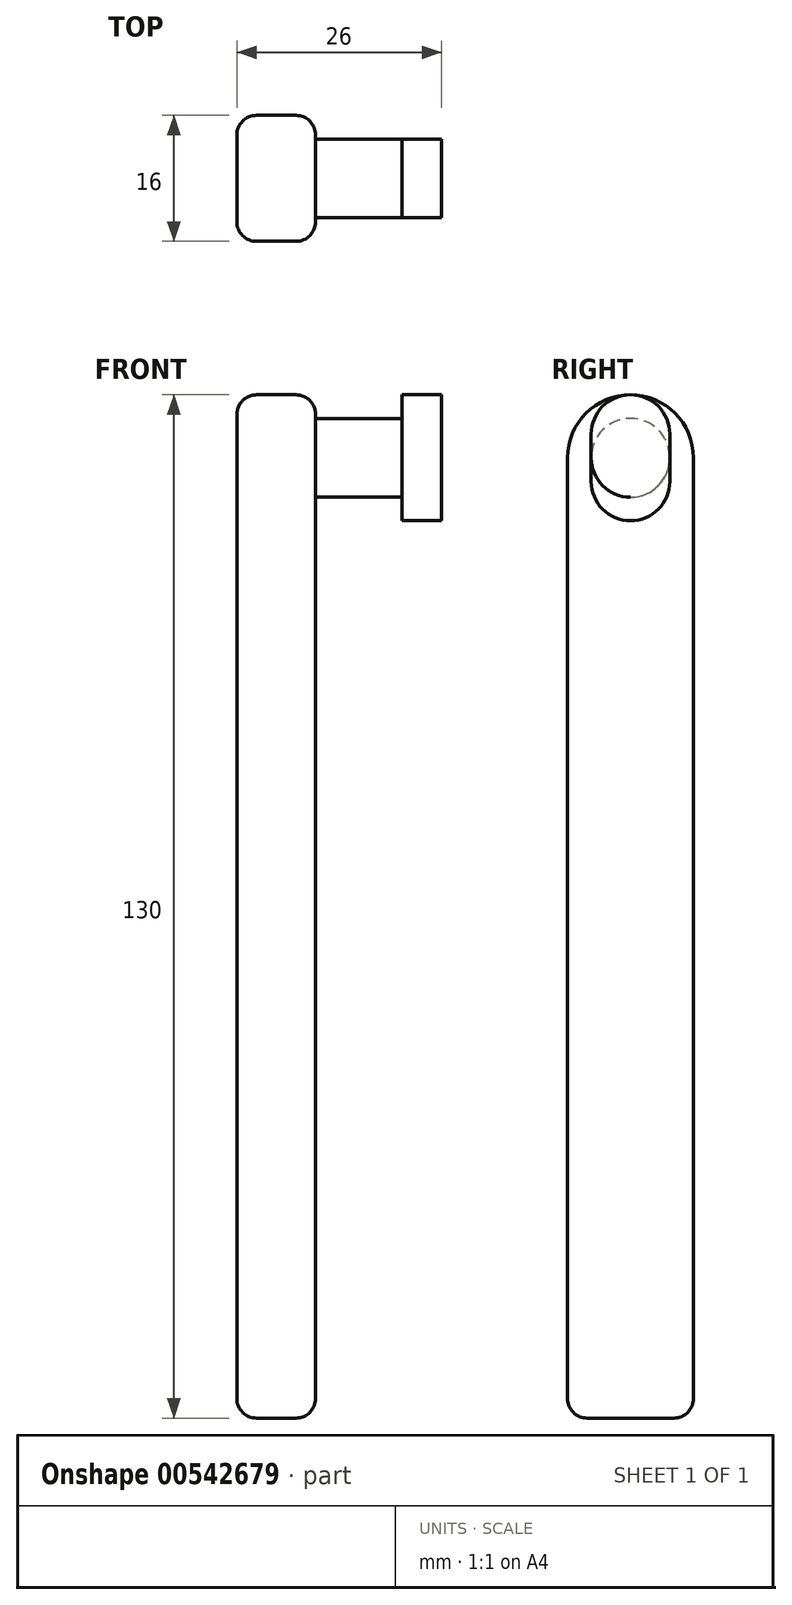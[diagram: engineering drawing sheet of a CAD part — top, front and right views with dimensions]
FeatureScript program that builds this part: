
annotation { "Feature Type Name" : "Feature", "Feature Type Description" : "" }
export const myFeature = defineFeature(function(context is Context, id is Id, definition is map)
    precondition{}
    {
        {
            var Q0;
            Q0=qCreatedBy(makeId("Right.planeOp"),FACE);
            var sketch = newSketch(context, id + "F0", { "sketchPlane" : qUnion([Q0])});
            skLineSegment(sketch, "E0.bottom", {"start": v(-8, 8) * mm, "end": v(8, 8) * mm});
            skLineSegment(sketch, "E0.top", {"start": v(-8, -122) * mm, "end": v(8, -122) * mm});
            skLineSegment(sketch, "E0.left", {"start": v(-8, 8) * mm, "end": v(-8, -122) * mm});
            skLineSegment(sketch, "E0.right", {"start": v(8, 8) * mm, "end": v(8, -122) * mm});
            skPoint(sketch, "E1", {"position": v(0, 8) * mm});
            skSolve(sketch);
        }
        {
            var Q0;
            Q0 = qSketchRegion(id + "F0", true);
            extrude(context, id + "F1", {"entities" : qUnion([Q0]), "depth" : 10 * mm, "offsetDistance" : 25 * mm});
        }
        {
            var Q0;
            Q0=makeQuery(id+"F1.opExtrude","CAP_FACE",FACE,{"disambiguationData":[OSD([sQuery(id+"F0.wireOp",EDGE,"E0.bottom"),sQuery(id+"F0.wireOp",EDGE,"E0.top"),sQuery(id+"F0.wireOp",EDGE,"E0.left"),sQuery(id+"F0.wireOp",EDGE,"E0.right")])],"isStart":false});
            var sketch = newSketch(context, id + "F2", { "sketchPlane" : qUnion([Q0])});
            skCircle(sketch, "E2", {"center": v(0, 0) * mm, "radius": 5 * mm});
            skSolve(sketch);
        }
        {
            var Q0;
            Q0 = qSketchRegion(id + "F2", true);
            extrude(context, id + "F3", {"entities" : qUnion([Q0]), "operationType" : NewBodyOperationType.ADD, "depth" : 11 * mm, "offsetDistance" : 25 * mm});
        }
        {
            var Q0;
            Q0=makeQuery(id+"F3.opExtrude","CAP_FACE",FACE,{"disambiguationData":[OSD([sQuery(id+"F2.wireOp",EDGE,"E2")])],"isStart":false});
            var sketch = newSketch(context, id + "F4", { "sketchPlane" : qUnion([Q0])});
            skLineSegment(sketch, "E3.bottom", {"start": v(-5, -8) * mm, "end": v(5, -8) * mm});
            skLineSegment(sketch, "E3.top", {"start": v(-5, 8) * mm, "end": v(5, 8) * mm});
            skLineSegment(sketch, "E3.left", {"start": v(-5, -8) * mm, "end": v(-5, 8) * mm});
            skLineSegment(sketch, "E3.right", {"start": v(5, -8) * mm, "end": v(5, 8) * mm});
            skPoint(sketch, "E3.middle", {"position": v(0, 0) * mm});
            skSolve(sketch);
        }
        {
            var Q0;
            Q0 = qSketchRegion(id + "F4", true);
            extrude(context, id + "F5", {"entities" : qUnion([Q0]), "operationType" : NewBodyOperationType.ADD, "depth" : 5 * mm, "offsetDistance" : 25 * mm});
        }
        {
            var Q0;
            Q0=makeQuery(id+"F1.opExtrude","SWEPT_EDGE",EDGE,{"disambiguationData":[OSD([sQuery(id+"F0.wireOp",EDGE,"E0.bottom"),sQuery(id+"F0.wireOp",EDGE,"E0.left")])]});
            var Q1;
            Q1=makeQuery(id+"F1.opExtrude","SWEPT_EDGE",EDGE,{"disambiguationData":[OSD([sQuery(id+"F0.wireOp",EDGE,"E0.bottom"),sQuery(id+"F0.wireOp",EDGE,"E0.right")])]});
            fillet(context, id + "F6", {"entities" : qUnion([Q0, Q1]), "radius" : 8 * mm, "tangentPropagation" : true, "allowEdgeOverflow" : false});
        }
        {
            var Q0;
            Q0=makeQuery(id+"F5.opExtrude","SWEPT_EDGE",EDGE,{"disambiguationData":[OSD([sQuery(id+"F4.wireOp",EDGE,"E3.top"),sQuery(id+"F4.wireOp",EDGE,"E3.left")])]});
            var Q1;
            Q1=makeQuery(id+"F5.opExtrude","SWEPT_EDGE",EDGE,{"disambiguationData":[OSD([sQuery(id+"F4.wireOp",EDGE,"E3.top"),sQuery(id+"F4.wireOp",EDGE,"E3.right")])]});
            var Q2;
            Q2=makeQuery(id+"F5.opExtrude","SWEPT_EDGE",EDGE,{"disambiguationData":[OSD([sQuery(id+"F4.wireOp",EDGE,"E3.bottom"),sQuery(id+"F4.wireOp",EDGE,"E3.left")])]});
            var Q3;
            Q3=makeQuery(id+"F5.opExtrude","SWEPT_EDGE",EDGE,{"disambiguationData":[OSD([sQuery(id+"F4.wireOp",EDGE,"E3.bottom"),sQuery(id+"F4.wireOp",EDGE,"E3.right")])]});
            fillet(context, id + "F7", {"entities" : qUnion([Q0, Q1, Q2, Q3]), "radius" : 5 * mm, "tangentPropagation" : true, "allowEdgeOverflow" : false});
        }
        {
            var Q0;
            {var subQ0=sQuery(id+"F4.wireOp",EDGE,"E3.right");var subQ1=sQuery(id+"F4.wireOp",EDGE,"E3.top");Q0=makeQuery(id+"F7.opFillet","BLEND_EDGE",EDGE,{"blendedFrom":[makeQuery(id+"F5.opExtrude","SWEPT_EDGE",EDGE,{"disambiguationData":[OSD([subQ1,subQ0])]}),makeQuery(id+"F5.opExtrude","CAP_FACE",FACE,{"disambiguationData":[OSD([sQuery(id+"F4.wireOp",EDGE,"E3.bottom"),subQ1,sQuery(id+"F4.wireOp",EDGE,"E3.left"),subQ0])],"isStart":false})],"blendedInto":[makeQuery(id+"F5.opExtrude","CAP_FACE",FACE,{"disambiguationData":[OSD([sQuery(id+"F4.wireOp",EDGE,"E3.bottom"),subQ1,sQuery(id+"F4.wireOp",EDGE,"E3.left"),subQ0])],"isStart":false})]});}
            var Q1;
            {var subQ0=sQuery(id+"F0.wireOp",EDGE,"E0.left");var subQ1=sQuery(id+"F0.wireOp",EDGE,"E0.bottom");Q1=makeQuery(id+"F6.opFillet","BLEND_EDGE",EDGE,{"blendedFrom":[makeQuery(id+"F1.opExtrude","SWEPT_EDGE",EDGE,{"disambiguationData":[OSD([subQ1,subQ0])]}),makeQuery(id+"F1.opExtrude","CAP_FACE",FACE,{"disambiguationData":[OSD([subQ1,sQuery(id+"F0.wireOp",EDGE,"E0.top"),subQ0,sQuery(id+"F0.wireOp",EDGE,"E0.right")])],"isStart":false})],"blendedInto":[makeQuery(id+"F1.opExtrude","CAP_FACE",FACE,{"disambiguationData":[OSD([subQ1,sQuery(id+"F0.wireOp",EDGE,"E0.top"),subQ0,sQuery(id+"F0.wireOp",EDGE,"E0.right")])],"isStart":false})]});}
            var Q2;
            {var subQ0=sQuery(id+"F0.wireOp",EDGE,"E0.left");var subQ1=sQuery(id+"F0.wireOp",EDGE,"E0.bottom");Q2=makeQuery(id+"F6.opFillet","BLEND_EDGE",EDGE,{"blendedFrom":[makeQuery(id+"F1.opExtrude","SWEPT_EDGE",EDGE,{"disambiguationData":[OSD([subQ1,subQ0])]}),makeQuery(id+"F1.opExtrude","CAP_FACE",FACE,{"disambiguationData":[OSD([subQ1,sQuery(id+"F0.wireOp",EDGE,"E0.top"),subQ0,sQuery(id+"F0.wireOp",EDGE,"E0.right")])],"isStart":true})],"blendedInto":[makeQuery(id+"F1.opExtrude","CAP_FACE",FACE,{"disambiguationData":[OSD([subQ1,sQuery(id+"F0.wireOp",EDGE,"E0.top"),subQ0,sQuery(id+"F0.wireOp",EDGE,"E0.right")])],"isStart":true})]});}
            var Q3;
            Q3=makeQuery(id+"F1.opExtrude","CAP_EDGE",EDGE,{"disambiguationData":[OSD([sQuery(id+"F0.wireOp",EDGE,"E0.top")])],"isStart":true});
            var Q4;
            Q4=makeQuery(id+"F1.opExtrude","SWEPT_EDGE",EDGE,{"disambiguationData":[OSD([sQuery(id+"F0.wireOp",EDGE,"E0.top"),sQuery(id+"F0.wireOp",EDGE,"E0.left")])]});
            var Q5;
            Q5=makeQuery(id+"F1.opExtrude","CAP_EDGE",EDGE,{"disambiguationData":[OSD([sQuery(id+"F0.wireOp",EDGE,"E0.top")])],"isStart":false});
            var Q6;
            Q6=makeQuery(id+"F1.opExtrude","SWEPT_EDGE",EDGE,{"disambiguationData":[OSD([sQuery(id+"F0.wireOp",EDGE,"E0.top"),sQuery(id+"F0.wireOp",EDGE,"E0.right")])]});
            fillet(context, id + "F8", {"entities" : qUnion([Q0, Q1, Q2, Q3, Q4, Q5, Q6]), "radius" : 2.5 * mm, "tangentPropagation" : true, "allowEdgeOverflow" : false});
        }
    });
